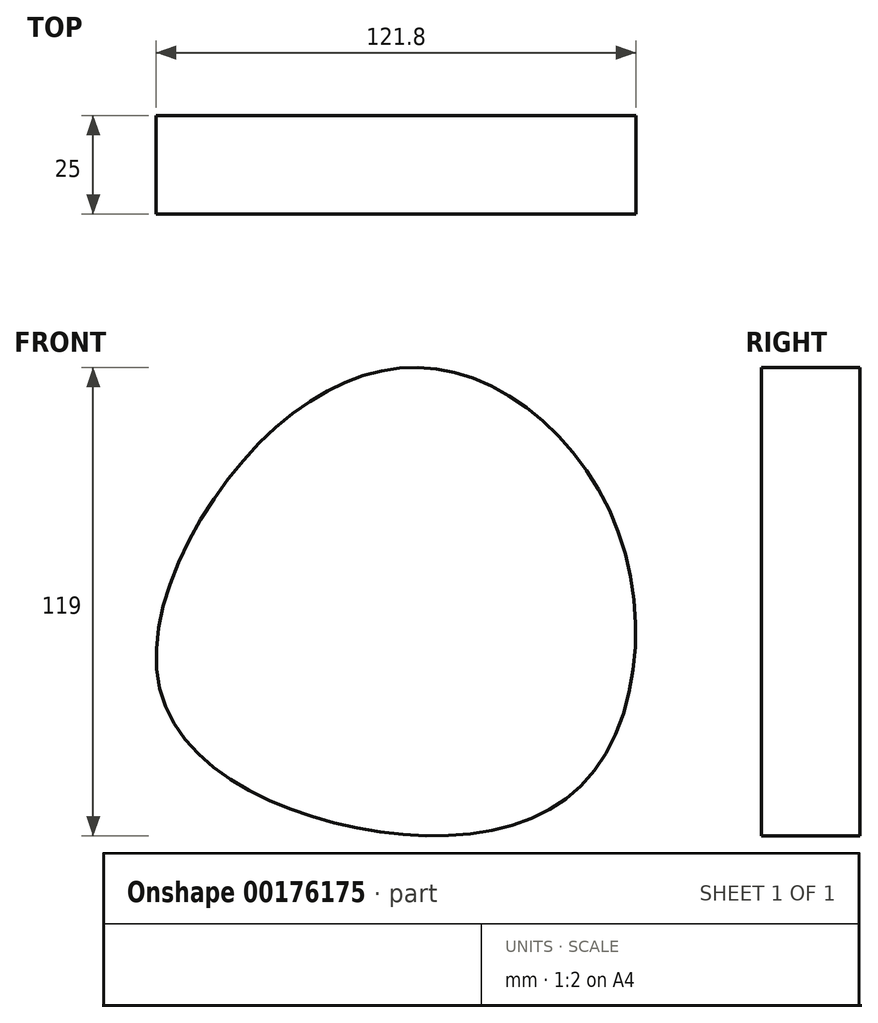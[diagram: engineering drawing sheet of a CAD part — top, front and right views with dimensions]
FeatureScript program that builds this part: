
annotation { "Feature Type Name" : "Feature", "Feature Type Description" : "" }
export const myFeature = defineFeature(function(context is Context, id is Id, definition is map)
    precondition{}
    {
        {
            var Q0;
            Q0=qCreatedBy(makeId("Front.planeOp"),FACE);
            var sketch = newSketch(context, id + "F0", { "sketchPlane" : qUnion([Q0])});
            skCircle(sketch, "E0.cCircle", {"center": v(0, 2.39) * mm, "radius": 31.7 * mm, "construction": true});
            skLineSegment(sketch, "E0.0", {"start": v(14.27, 64.17) * mm, "end": v(46.37, -40.87) * mm});
            skLineSegment(sketch, "E0.1", {"start": v(46.37, -40.87) * mm, "end": v(-60.64, -16.14) * mm});
            skLineSegment(sketch, "E0.2", {"start": v(-60.64, -16.14) * mm, "end": v(14.27, 64.17) * mm});
            skPoint(sketch, "E0.0.midPoint", {"position": v(30.32, 11.65) * mm});
            skFitSpline(sketch, "E1", {"points": [v(14.27, 64.17) * mm, v(-33.69, 47.87) * mm, v(-60.64, -16.14) * mm, v(-14.6, -50.68) * mm, v(46.37, -40.87) * mm, v(56.43, 22.04) * mm, v(14.27, 64.17) * mm]});
            skSolve(sketch);
        }
        {
            var Q0;
            Q0 = qSketchRegion(id + "F0", true);
            extrude(context, id + "F1", {"entities" : qUnion([Q0]), "depth" : 25 * mm});
        }
    });
